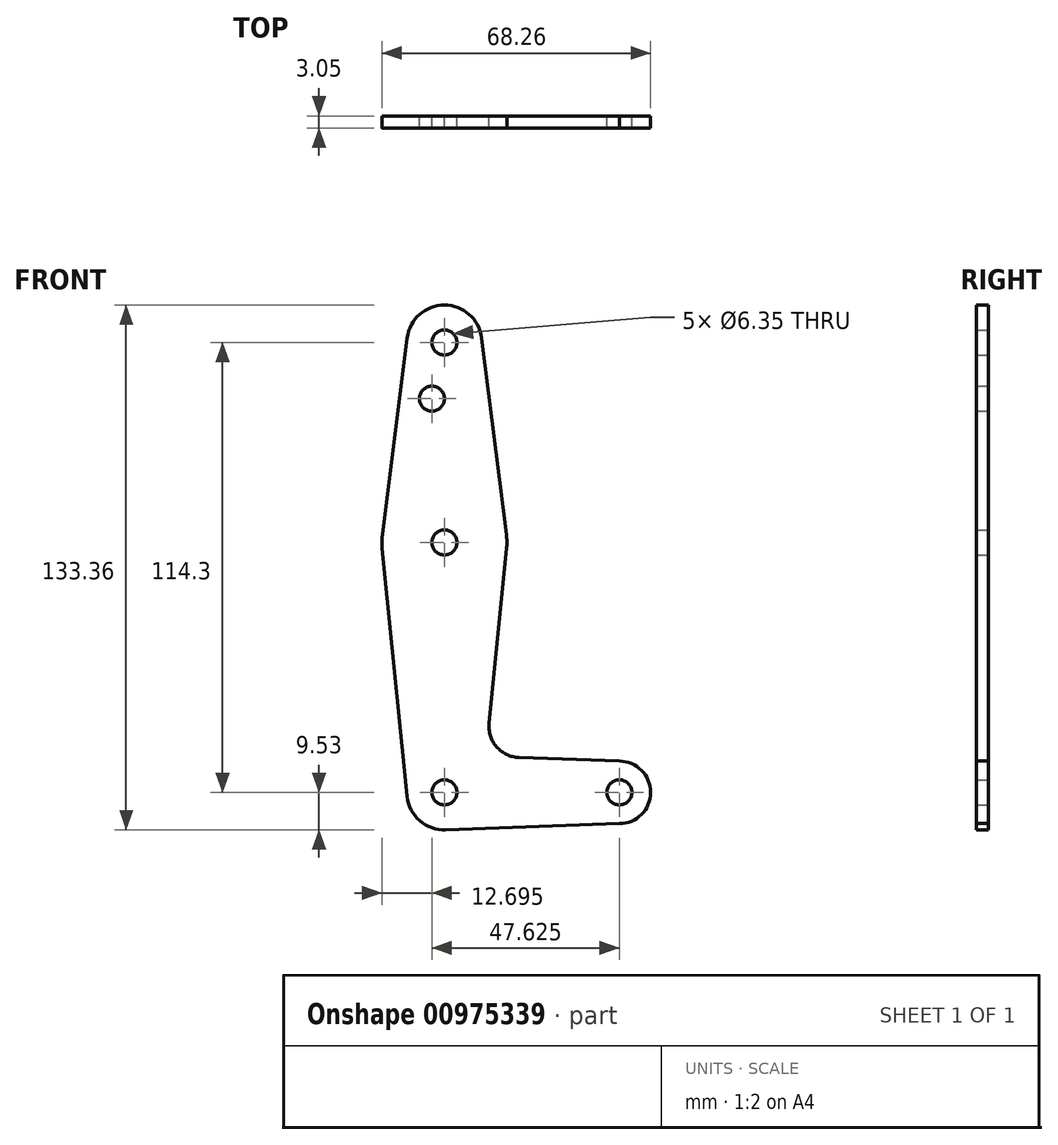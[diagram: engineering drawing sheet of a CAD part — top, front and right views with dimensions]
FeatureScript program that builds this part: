
annotation { "Feature Type Name" : "Feature", "Feature Type Description" : "" }
export const myFeature = defineFeature(function(context is Context, id is Id, definition is map)
    precondition{}
    {
        {
            var Q0;
            Q0=qCreatedBy(makeId("Front.planeOp"),FACE);
            var sketch = newSketch(context, id + "F0", { "sketchPlane" : qUnion([Q0])});
            skLineSegment(sketch, "E0", {"start": v(0, 0) * mm, "end": v(0, 114.3) * mm, "construction": true});
            skLineSegment(sketch, "E1", {"start": v(0, 0) * mm, "end": v(44.45, 0) * mm, "construction": true});
            skCircle(sketch, "E2", {"center": v(0, 114.3) * mm, "radius": 9.53 * mm});
            skCircle(sketch, "E3", {"center": v(0, 63.5) * mm, "radius": 15.88 * mm});
            skCircle(sketch, "E4", {"center": v(0, 0) * mm, "radius": 9.53 * mm});
            skCircle(sketch, "E5", {"center": v(44.45, 0) * mm, "radius": 7.94 * mm});
            skLineSegment(sketch, "E6", {"start": v(9.45, 115.5) * mm, "end": v(15.75, 65.48) * mm});
            skLineSegment(sketch, "E7", {"start": v(-9.45, 115.5) * mm, "end": v(-15.75, 65.48) * mm});
            skLineSegment(sketch, "E8", {"start": v(44.45, 7.94) * mm, "end": v(18.97, 8.85) * mm});
            skLineSegment(sketch, "E9", {"start": v(44.45, -7.94) * mm, "end": v(0, -9.53) * mm});
            skLineSegment(sketch, "E10", {"start": v(-15.8, 61.91) * mm, "end": v(-9.48, -0.95) * mm});
            skLineSegment(sketch, "E11", {"start": v(15.8, 61.91) * mm, "end": v(11.34, 17.6) * mm});
            skCircle(sketch, "E12", {"center": v(0, 114.3) * mm, "radius": 3.18 * mm});
            skCircle(sketch, "E13", {"center": v(-3.18, 100.03) * mm, "radius": 3.18 * mm});
            skCircle(sketch, "E14", {"center": v(0, 63.5) * mm, "radius": 3.18 * mm});
            skCircle(sketch, "E15", {"center": v(0, 0) * mm, "radius": 3.18 * mm});
            skCircle(sketch, "E16", {"center": v(44.45, 0) * mm, "radius": 3.18 * mm});
            skPoint(sketch, "E17.newPointB", {"position": v(0, 9.53) * mm});
            skArc(sketch, "E17.filletArc", {"start": v(11.34, 17.6) * mm, "mid": v(13.26, 11.57) * mm, "end": v(18.97, 8.85) * mm});
            skSolve(sketch);
        }
        {
            var Q0;
            Q0=makeQuery(id+"F0.imprint","IMPRINT",FACE,{"disambiguationData":[TD([[makeQuery(id+"F0.imprint","IMPRINT",EDGE,{"derivedFrom":sQuery(id+"F0.wireOp",EDGE,"E12")}),-1.0]])]});
            var Q1;
            {var subQ0=sQuery(id+"F0.wireOp",EDGE,"E6");Q1=makeQuery(id+"F0.imprint","IMPRINT",FACE,{"disambiguationData":[TD([[makeQuery(id+"F0.imprint","IMPRINT",EDGE,{"derivedFrom":subQ0}),-1.0]])]});}
            var Q2;
            Q2=makeQuery(id+"F0.imprint","IMPRINT",FACE,{"disambiguationData":[TD([[makeQuery(id+"F0.imprint","IMPRINT",EDGE,{"derivedFrom":sQuery(id+"F0.wireOp",EDGE,"E14")}),-1.0]])]});
            var Q3;
            {var subQ0=sQuery(id+"F0.wireOp",EDGE,"E8");Q3=makeQuery(id+"F0.imprint","IMPRINT",FACE,{"disambiguationData":[TD([[makeQuery(id+"F0.imprint","IMPRINT",EDGE,{"derivedFrom":subQ0}),1.0]])]});}
            var Q4;
            Q4=makeQuery(id+"F0.imprint","IMPRINT",FACE,{"disambiguationData":[TD([[makeQuery(id+"F0.imprint","IMPRINT",EDGE,{"derivedFrom":sQuery(id+"F0.wireOp",EDGE,"E15")}),-1.0]])]});
            var Q5;
            Q5=makeQuery(id+"F0.imprint","IMPRINT",FACE,{"disambiguationData":[TD([[makeQuery(id+"F0.imprint","IMPRINT",EDGE,{"derivedFrom":sQuery(id+"F0.wireOp",EDGE,"E16")}),-1.0]])]});
            extrude(context, id + "F1", {"entities" : qUnion([Q0, Q1, Q2, Q3, Q4, Q5]), "depth" : 3.05 * mm, "offsetDistance" : 25.4 * mm});
        }
    });
